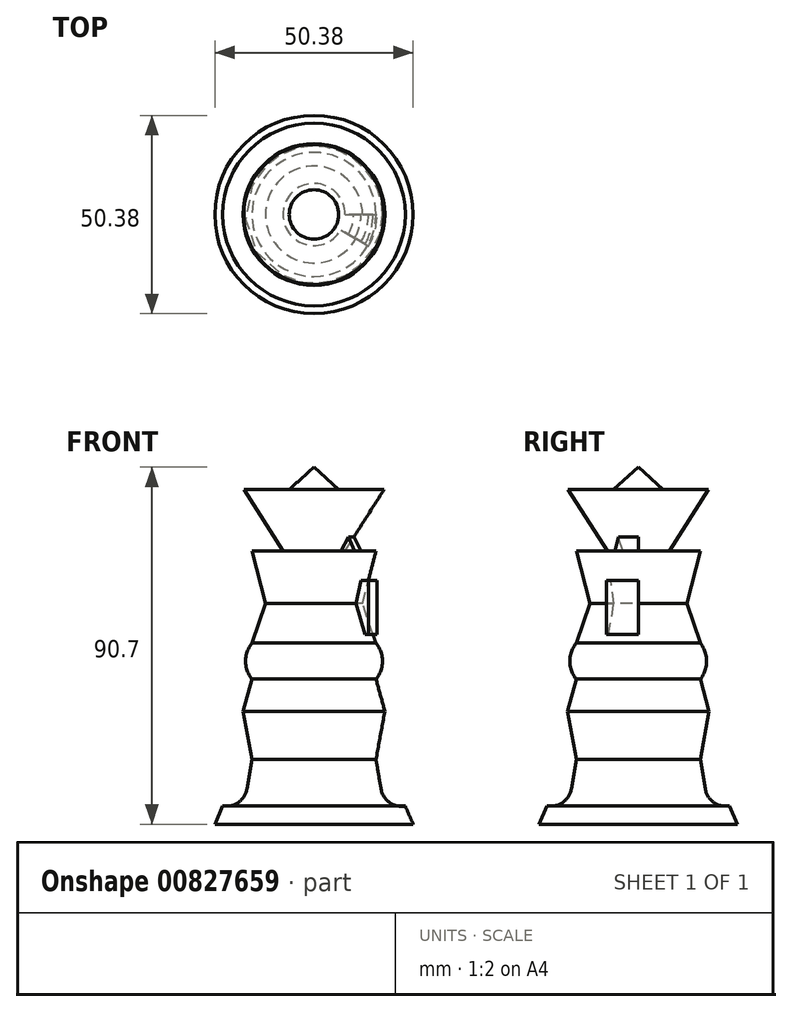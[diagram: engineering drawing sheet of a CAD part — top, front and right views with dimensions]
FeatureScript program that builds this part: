
annotation { "Feature Type Name" : "Feature", "Feature Type Description" : "" }
export const myFeature = defineFeature(function(context is Context, id is Id, definition is map)
    precondition{}
    {
        {
            var Q0;
            Q0=qCreatedBy(makeId("Front.planeOp"),FACE);
            var sketch = newSketch(context, id + "F0", { "sketchPlane" : qUnion([Q0])});
            skLineSegment(sketch, "E0", {"start": v(0, -17.92) * mm, "end": v(25.19, -17.92) * mm});
            skLineSegment(sketch, "E1", {"start": v(25.19, -17.92) * mm, "end": v(23.2, -13.34) * mm});
            skArc(sketch, "E2", {"start": v(17.02, -8.96) * mm, "mid": v(19.2, -12.43) * mm, "end": v(23.2, -13.34) * mm});
            skLineSegment(sketch, "E3", {"start": v(17.02, -8.96) * mm, "end": v(15.75, -1.47) * mm});
            skLineSegment(sketch, "E4", {"start": v(15.75, -1.47) * mm, "end": v(18.02, 10.77) * mm});
            skLineSegment(sketch, "E5", {"start": v(18.02, 10.77) * mm, "end": v(15.75, 18.92) * mm});
            skArc(sketch, "E6", {"start": v(15.75, 18.92) * mm, "mid": v(17.39, 23.5) * mm, "end": v(15.75, 28.08) * mm});
            skLineSegment(sketch, "E7", {"start": v(15.75, 28.08) * mm, "end": v(12.33, 38.15) * mm});
            skLineSegment(sketch, "E8", {"start": v(12.33, 38.15) * mm, "end": v(15.75, 51.49) * mm});
            skLineSegment(sketch, "E9", {"start": v(15.75, 51.49) * mm, "end": v(0, 51.49) * mm});
            skLineSegment(sketch, "E10", {"start": v(7.88, 51.49) * mm, "end": v(17.82, 67.1) * mm});
            skLineSegment(sketch, "E11", {"start": v(17.82, 67.1) * mm, "end": v(0, 67.1) * mm});
            skLineSegment(sketch, "E12", {"start": v(0, 72.78) * mm, "end": v(6.3, 67.1) * mm});
            skLineSegment(sketch, "E13", {"start": v(0, 72.78) * mm, "end": v(0, -17.92) * mm});
            skSolve(sketch);
        }
        {
            var Q0;
            {var subQ3=sQuery(id+"F0.wireOp",EDGE,"E12");Q0=makeQuery(id+"F0.imprint","IMPRINT",FACE,{"disambiguationData":[TD([[makeQuery(id+"F0.imprint","IMPRINT",EDGE,{"derivedFrom":subQ3}),-1.0]])]});}
            var Q1;
            {var subQ4=sQuery(id+"F0.wireOp",EDGE,"E10");Q1=makeQuery(id+"F0.imprint","IMPRINT",FACE,{"disambiguationData":[TD([[makeQuery(id+"F0.imprint","IMPRINT",EDGE,{"derivedFrom":subQ4}),1.0]])]});}
            var Q2;
            {var subQ3=sQuery(id+"F0.wireOp",EDGE,"E0");Q2=makeQuery(id+"F0.imprint","IMPRINT",FACE,{"disambiguationData":[TD([[makeQuery(id+"F0.imprint","IMPRINT",EDGE,{"derivedFrom":subQ3}),1.0]])]});}
            var Q3;
            Q3=sQuery(id+"F0.wireOp",EDGE,"E13");
            revolve(context, id + "F1", {"surfaceOperationType" : NewSurfaceOperationType.NEW, "entities" : qUnion([Q0, Q1, Q2]), "axis" : qUnion([Q3]), "revolveType" : RevolveType.FULL});
        }
        {
            var Q0;
            Q0=qCreatedBy(makeId("Front.planeOp"),FACE);
            var sketch = newSketch(context, id + "F2", { "sketchPlane" : qUnion([Q0])});
            skLineSegment(sketch, "E14.bottom", {"start": v(11.65, 44) * mm, "end": v(16.03, 44) * mm});
            skLineSegment(sketch, "E14.top", {"start": v(11.65, 30.27) * mm, "end": v(16.03, 30.27) * mm});
            skLineSegment(sketch, "E14.left", {"start": v(11.65, 44) * mm, "end": v(11.65, 30.27) * mm});
            skLineSegment(sketch, "E14.right", {"start": v(16.03, 44) * mm, "end": v(16.03, 30.27) * mm});
            skSolve(sketch);
        }
        {
            var Q0;
            Q0=makeQuery(id+"F2.imprint","IMPRINT",FACE,{"disambiguationData":[TD([[makeQuery(id+"F2.imprint","IMPRINT",EDGE,{"derivedFrom":sQuery(id+"F2.wireOp",EDGE,"E14.bottom")}),-1.0]])]});
            var Q1;
            Q1=sQuery(id+"F0.wireOp",EDGE,"E13");
            revolve(context, id + "F3", {"operationType" : NewBodyOperationType.ADD, "surfaceOperationType" : NewSurfaceOperationType.NEW, "entities" : qUnion([Q0]), "axis" : qUnion([Q1]), "revolveType" : RevolveType.ONE_DIRECTION, "angle" : 30 * degree});
        }
        {
            var Q0;
            Q0=qCreatedBy(makeId("Front.planeOp"),FACE);
            var sketch = newSketch(context, id + "F4", { "sketchPlane" : qUnion([Q0])});
            skLineSegment(sketch, "E15", {"start": v(8.26, 58.54) * mm, "end": v(12.84, 49.78) * mm});
            skLineSegment(sketch, "E16", {"start": v(12.84, 49.78) * mm, "end": v(6.67, 49.78) * mm});
            skLineSegment(sketch, "E17", {"start": v(6.67, 49.78) * mm, "end": v(8.26, 58.54) * mm});
            skSolve(sketch);
        }
        {
            var Q0;
            Q0=makeQuery(id+"F4.imprint","IMPRINT",FACE,{"disambiguationData":[TD([[makeQuery(id+"F4.imprint","IMPRINT",EDGE,{"derivedFrom":sQuery(id+"F4.wireOp",EDGE,"E15")}),-1.0]])]});
            var Q1;
            Q1=sQuery(id+"F0.wireOp",EDGE,"E13");
            revolve(context, id + "F5", {"operationType" : NewBodyOperationType.ADD, "surfaceOperationType" : NewSurfaceOperationType.NEW, "entities" : qUnion([Q0]), "axis" : qUnion([Q1]), "revolveType" : RevolveType.ONE_DIRECTION, "angle" : 30 * degree});
        }
    });
